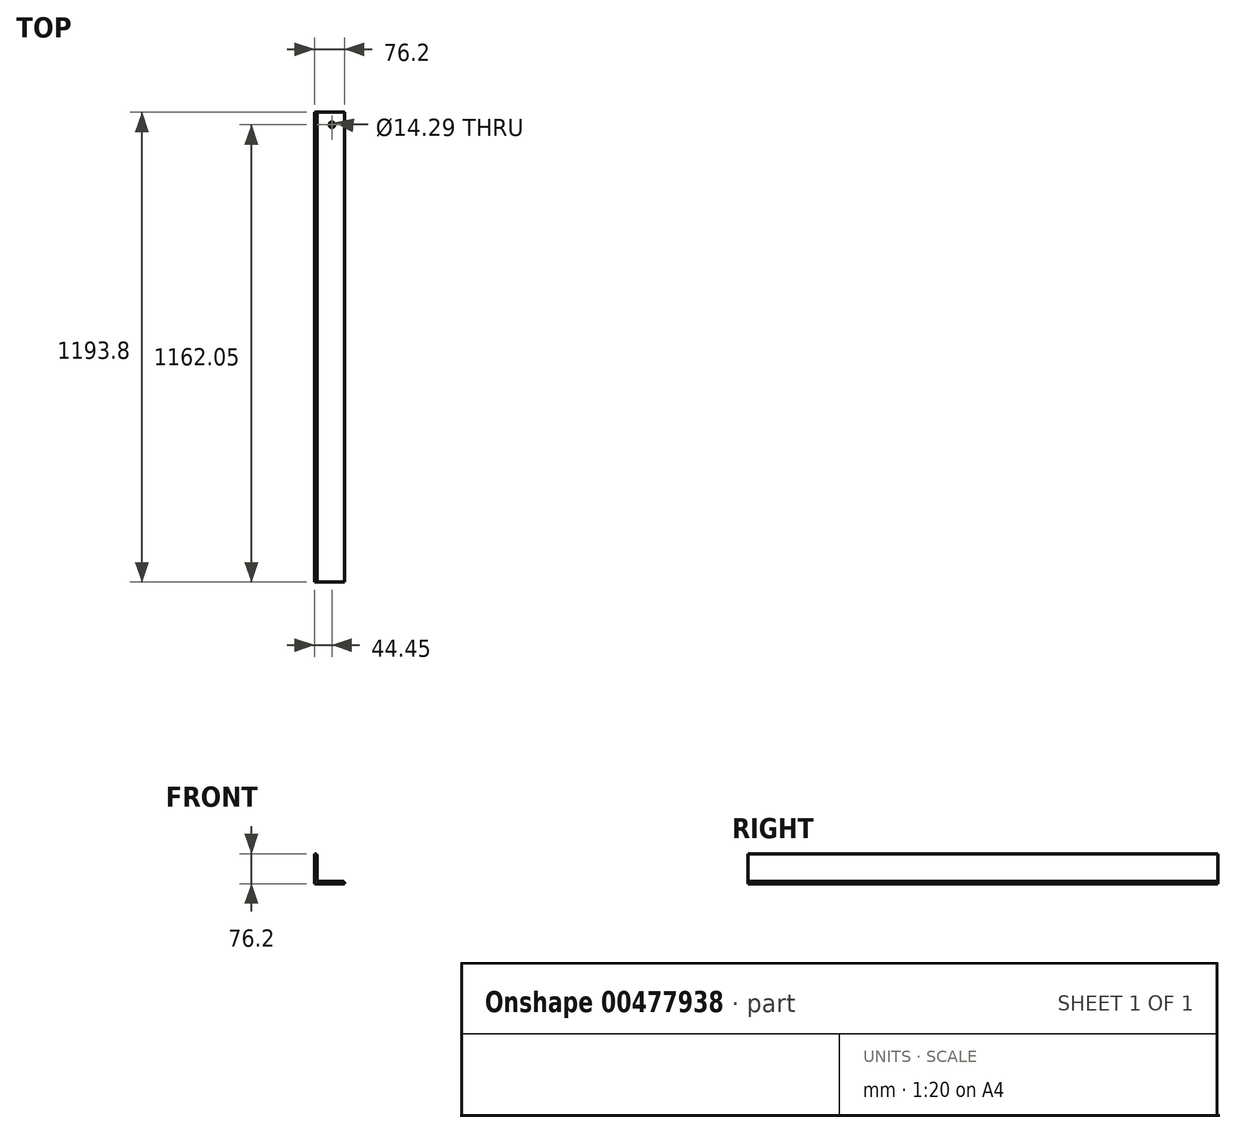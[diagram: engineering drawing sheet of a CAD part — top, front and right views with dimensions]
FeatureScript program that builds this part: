
annotation { "Feature Type Name" : "Feature", "Feature Type Description" : "" }
export const myFeature = defineFeature(function(context is Context, id is Id, definition is map)
    precondition{}
    {
        {
            var Q0;
            Q0=qCreatedBy(makeId("Front.planeOp"),FACE);
            var sketch = newSketch(context, id + "F0", { "sketchPlane" : qUnion([Q0])});
            skLineSegment(sketch, "E0.bottom", {"start": v(38.1, -38.1) * mm, "end": v(-38.1, -38.1) * mm});
            skLineSegment(sketch, "E0.top", {"start": v(-31.75, 38.1) * mm, "end": v(-38.1, 38.1) * mm});
            skLineSegment(sketch, "E0.left", {"start": v(38.1, -38.1) * mm, "end": v(38.1, -31.75) * mm});
            skLineSegment(sketch, "E0.right", {"start": v(-38.1, -38.1) * mm, "end": v(-38.1, 38.1) * mm});
            skPoint(sketch, "E0.middle", {"position": v(0, 0) * mm});
            skLineSegment(sketch, "E1.0", {"start": v(-31.75, -31.75) * mm, "end": v(-31.75, 38.1) * mm});
            skLineSegment(sketch, "E2.0", {"start": v(38.1, -31.75) * mm, "end": v(-31.75, -31.75) * mm});
            skPoint(sketch, "E3.orphan", {"position": v(38.1, 38.1) * mm});
            skSolve(sketch);
        }
        {
            var Q0;
            Q0 = qSketchRegion(id + "F0", true);
            extrude(context, id + "F1", {"entities" : qUnion([Q0]), "endBound" : BoundingType.SYMMETRIC, "depth" : 1193.8 * mm});
        }
        {
            var Q0;
            Q0=makeQuery(id+"F1.opExtrude","SWEPT_EDGE",EDGE,{"disambiguationData":[OSD([sQuery(id+"F0.wireOp",EDGE,"E0.top"),sQuery(id+"F0.wireOp",EDGE,"E1.0")])]});
            var Q1;
            Q1=makeQuery(id+"F1.opExtrude","SWEPT_EDGE",EDGE,{"disambiguationData":[OSD([sQuery(id+"F0.wireOp",EDGE,"E1.0"),sQuery(id+"F0.wireOp",EDGE,"E2.0")])]});
            var Q2;
            Q2=makeQuery(id+"F1.opExtrude","SWEPT_EDGE",EDGE,{"disambiguationData":[OSD([sQuery(id+"F0.wireOp",EDGE,"E0.left"),sQuery(id+"F0.wireOp",EDGE,"E2.0")])]});
            fillet(context, id + "F2", {"entities" : qUnion([Q0, Q1, Q2]), "radius" : 5.08 * mm, "tangentPropagation" : true, "allowEdgeOverflow" : false});
        }
        {
            var Q0;
            Q0=makeQuery(id+"F1.opExtrude","SWEPT_FACE",FACE,{"disambiguationData":[OSD([sQuery(id+"F0.wireOp",EDGE,"E0.bottom")])]});
            var sketch = newSketch(context, id + "F3", { "sketchPlane" : qUnion([Q0])});
            skCircle(sketch, "E4", {"center": v(6.35, -565.15) * mm, "radius": 7.14 * mm});
            skSolve(sketch);
        }
        {
            var Q0;
            Q0 = qSketchRegion(id + "F3", true);
            extrude(context, id + "F4", {"entities" : qUnion([Q0]), "operationType" : NewBodyOperationType.REMOVE, "oppositeDirection" : true, "depth" : 25.4 * mm});
        }
    });
